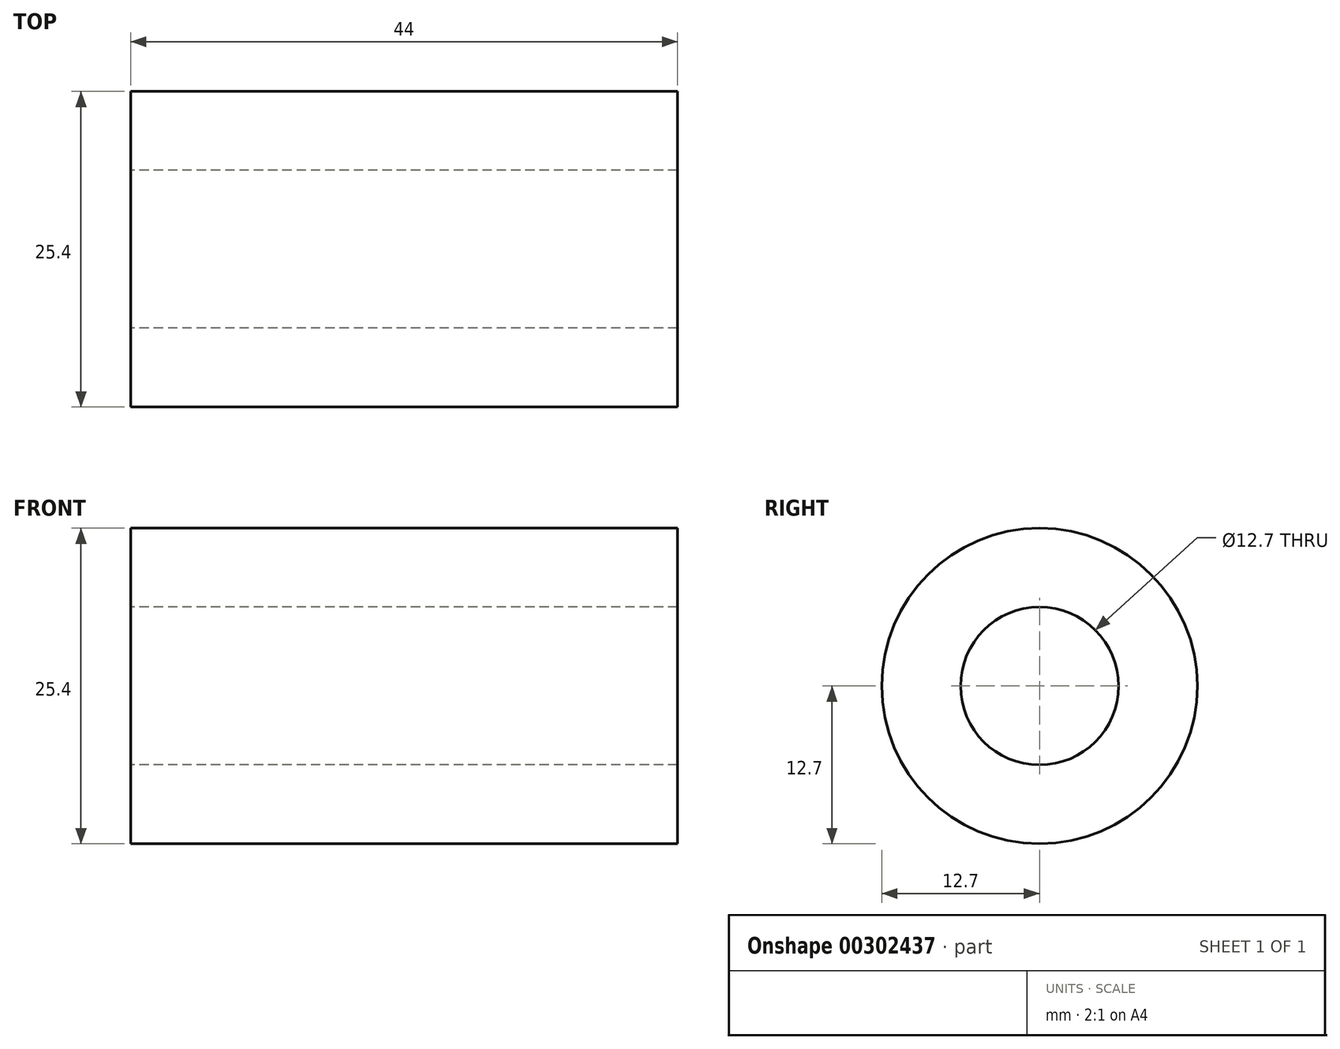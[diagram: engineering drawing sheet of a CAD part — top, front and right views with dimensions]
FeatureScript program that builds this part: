
annotation { "Feature Type Name" : "Feature", "Feature Type Description" : "" }
export const myFeature = defineFeature(function(context is Context, id is Id, definition is map)
    precondition{}
    {
        {
            var Q0;
            Q0=qCreatedBy(makeId("Right.planeOp"),FACE);
            var sketch = newSketch(context, id + "F0", { "sketchPlane" : qUnion([Q0])});
            skCircle(sketch, "E0", {"center": v(0, 0) * mm, "radius": 12.7 * mm});
            skCircle(sketch, "E1", {"center": v(0, 0) * mm, "radius": 6.35 * mm});
            skLineSegment(sketch, "E2", {"start": v(-12.44, 2.54) * mm, "end": v(-5.82, 2.54) * mm});
            skLineSegment(sketch, "E3", {"start": v(-12.44, -2.54) * mm, "end": v(-5.82, -2.54) * mm});
            skLineSegment(sketch, "E4", {"start": v(-2.54, -12.44) * mm, "end": v(-2.54, -5.82) * mm});
            skLineSegment(sketch, "E5", {"start": v(2.54, -12.44) * mm, "end": v(2.54, -5.82) * mm});
            skLineSegment(sketch, "E6", {"start": v(5.82, 2.54) * mm, "end": v(12.44, 2.54) * mm});
            skLineSegment(sketch, "E7", {"start": v(5.82, -2.54) * mm, "end": v(12.44, -2.54) * mm});
            skLineSegment(sketch, "E8", {"start": v(-2.54, 12.44) * mm, "end": v(-2.54, 5.82) * mm});
            skLineSegment(sketch, "E9", {"start": v(2.54, 5.82) * mm, "end": v(2.54, 12.44) * mm});
            skSolve(sketch);
        }
        {
            var Q0;
            Q0 = qSketchRegion(id + "F0", true);
            var Q1;
            Q1 = qSketchRegion(id + "FQN2oRWplfWn9WT_0", true);
            extrude(context, id + "F1", {"entities" : qUnion([Q0, Q1]), "depth" : 25.4 * mm});
        }
        {
            var Q0;
            Q0 = qSketchRegion(id + "F0", true);
            extrude(context, id + "F2", {"entities" : qUnion([Q0]), "operationType" : NewBodyOperationType.ADD, "endBound" : BoundingType.THROUGH_ALL, "depth" : 25.4 * mm});
        }
    });
